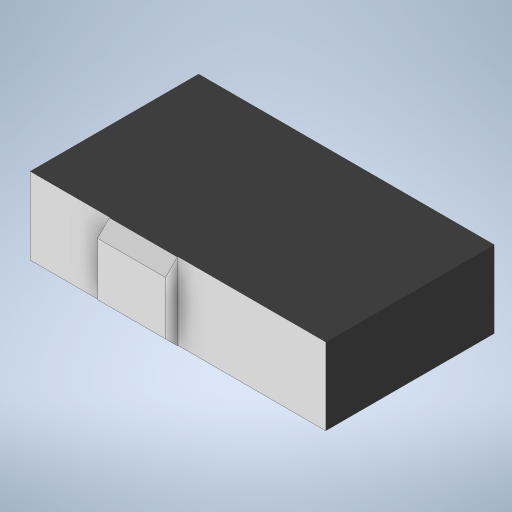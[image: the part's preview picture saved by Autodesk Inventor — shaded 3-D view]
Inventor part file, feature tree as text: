
AUTODESK INVENTOR PART (.ipt)
format: ipt  version: 2023 (Build 270158000, 158)  size: 224,768 bytes
history: native  units: mm
features: extrude x2, sketch x2, other x1, chamfer x1, projected_geometry x1
ambient origin geometry x8: Origin, YZ Plane, XZ Plane, XY Plane, X Axis, Y Axis, Z Axis, Center Point
bodies: Body1 (feature_tree)
feature tree (7):
  other  "Bryła1"
  extrude  "Wyciągnięcie proste1"  Depth=10.0mm
  extrude  "Wyciągnięcie proste2"  Depth=5.7mm
  chamfer  "Faza1"  Distance=2.6mm
  sketch  "Szkic1"
  sketch  "Szkic2"
  projected_geometry  "Pętla rzutowana1"
